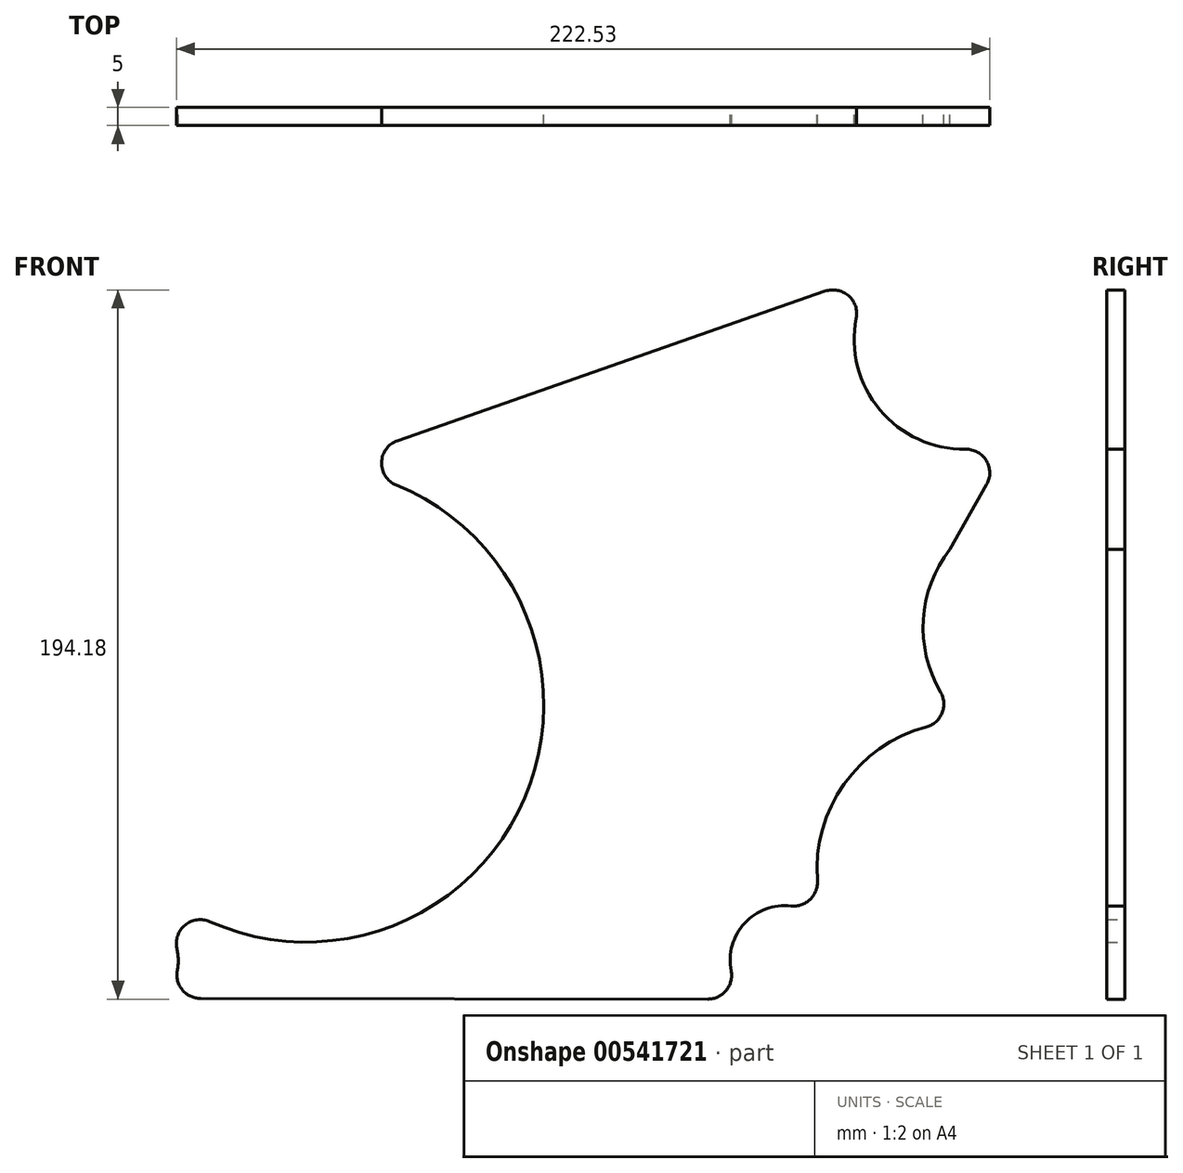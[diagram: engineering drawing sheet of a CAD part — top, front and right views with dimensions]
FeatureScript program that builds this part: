
annotation { "Feature Type Name" : "Feature", "Feature Type Description" : "" }
export const myFeature = defineFeature(function(context is Context, id is Id, definition is map)
    precondition{}
    {
        {
            var Q0;
            Q0=qCreatedBy(makeId("Front.planeOp"),FACE);
            var sketch = newSketch(context, id + "F0", { "sketchPlane" : qUnion([Q0])});
            skCircle(sketch, "E0", {"center": v(0, 0) * mm, "radius": 60 * mm});
            skCircle(sketch, "E1", {"center": v(-24.58, 0) * mm, "radius": 5 * mm});
            skCircle(sketch, "E2.1.0", {"center": v(-12.3, -21.3) * mm, "radius": 5 * mm});
            skCircle(sketch, "E2.2.0", {"center": v(12.3, -21.3) * mm, "radius": 5 * mm});
            skCircle(sketch, "E2.3.0", {"center": v(24.58, 0) * mm, "radius": 5 * mm});
            skCircle(sketch, "E2.4.0", {"center": v(12.3, 21.3) * mm, "radius": 5 * mm});
            skCircle(sketch, "E2.5.0", {"center": v(-12.3, 21.3) * mm, "radius": 5 * mm});
            skLineSegment(sketch, "E3", {"start": v(0, 0) * mm, "end": v(78.97, 13.92) * mm, "construction": true});
            skArc(sketch, "E4", {"start": v(44.32, 7.81) * mm, "mid": v(50.1, 3.76) * mm, "end": v(54.16, 9.55) * mm});
            skLineSegment(sketch, "E5", {"start": v(0, 0) * mm, "end": v(13.1, 74.28) * mm, "construction": true});
            skArc(sketch, "E6", {"start": v(9.55, 54.16) * mm, "mid": v(3.76, 50.1) * mm, "end": v(7.81, 44.32) * mm});
            skArc(sketch, "E7", {"start": v(9.55, 54.16) * mm, "mid": v(38.9, 38.9) * mm, "end": v(54.16, 9.55) * mm});
            skArc(sketch, "E8", {"start": v(7.81, 44.32) * mm, "mid": v(31.82, 31.82) * mm, "end": v(44.32, 7.81) * mm});
            skArc(sketch, "E9.MirrorCS", {"start": v(-9.55, 54.16) * mm, "mid": v(-38.9, 38.9) * mm, "end": v(-54.16, 9.55) * mm});
            skArc(sketch, "E10.MirrorCS", {"start": v(-7.81, 44.32) * mm, "mid": v(-31.82, 31.82) * mm, "end": v(-44.32, 7.81) * mm});
            skArc(sketch, "E11.MirrorCS", {"start": v(-44.32, 7.81) * mm, "mid": v(-50.1, 3.76) * mm, "end": v(-54.16, 9.55) * mm});
            skArc(sketch, "E12.MirrorCS", {"start": v(-9.55, 54.16) * mm, "mid": v(-3.76, 50.1) * mm, "end": v(-7.81, 44.32) * mm});
            skArc(sketch, "E13.MirrorCS", {"start": v(-7.81, -44.32) * mm, "mid": v(-31.82, -31.82) * mm, "end": v(-44.32, -7.81) * mm});
            skArc(sketch, "E14.MirrorCS", {"start": v(-9.55, -54.16) * mm, "mid": v(-38.9, -38.9) * mm, "end": v(-54.16, -9.55) * mm});
            skArc(sketch, "E15.MirrorCS", {"start": v(-44.32, -7.81) * mm, "mid": v(-50.1, -3.76) * mm, "end": v(-54.16, -9.55) * mm});
            skArc(sketch, "E16.MirrorCS", {"start": v(-9.55, -54.16) * mm, "mid": v(-3.76, -50.1) * mm, "end": v(-7.81, -44.32) * mm});
            skArc(sketch, "E17.MirrorCS", {"start": v(9.55, -54.16) * mm, "mid": v(3.76, -50.1) * mm, "end": v(7.81, -44.32) * mm});
            skArc(sketch, "E18.MirrorCS", {"start": v(7.81, -44.32) * mm, "mid": v(31.82, -31.82) * mm, "end": v(44.32, -7.81) * mm});
            skArc(sketch, "E19.MirrorCS", {"start": v(9.55, -54.16) * mm, "mid": v(38.9, -38.9) * mm, "end": v(54.16, -9.55) * mm});
            skArc(sketch, "E20.MirrorCS", {"start": v(44.32, -7.81) * mm, "mid": v(50.1, -3.76) * mm, "end": v(54.16, -9.55) * mm});
            skLineSegment(sketch, "E21", {"start": v(180, 112.63) * mm, "end": v(180, -76.66) * mm, "construction": true});
            skLineSegment(sketch, "E22", {"start": v(-74.83, 0) * mm, "end": v(210.53, 0) * mm, "construction": true});
            skCircle(sketch, "E23", {"center": v(180, 100) * mm, "radius": 25 * mm});
            skCircle(sketch, "E24", {"center": v(180, -45) * mm, "radius": 35 * mm});
            skArc(sketch, "E25", {"start": v(-21.46, 61.35) * mm, "mid": v(-53.01, 37.62) * mm, "end": v(-65, 0) * mm});
            skArc(sketch, "E26", {"start": v(150.52, 105.8) * mm, "mid": v(156.92, 80.75) * mm, "end": v(180.43, 69.95) * mm});
            skArc(sketch, "E27", {"start": v(169.62, -6.12) * mm, "mid": v(147.16, -21.75) * mm, "end": v(139.88, -48.13) * mm});
            skLineSegment(sketch, "E28", {"start": v(-21.46, 61.35) * mm, "end": v(170.08, 128.36) * mm});
            skLineSegment(sketch, "E29", {"start": v(24.98, 72.3) * mm, "end": v(142, 113.2) * mm});
            skPoint(sketch, "E30.visualSharp", {"position": v(3.8, 64.89) * mm});
            skArc(sketch, "E30.filletArc", {"start": v(24.98, 72.3) * mm, "mid": v(20.62, 66.33) * mm, "end": v(24.66, 60.14) * mm});
            skPoint(sketch, "E31.visualSharp", {"position": v(156, 118.1) * mm});
            skArc(sketch, "E31.filletArc", {"start": v(150.52, 105.8) * mm, "mid": v(148.4, 111.97) * mm, "end": v(142, 113.2) * mm});
            skArc(sketch, "E32", {"start": v(180, 39.38) * mm, "mid": v(175, 12.66) * mm, "end": v(193.63, -7.13) * mm});
            skLineSegment(sketch, "E33.trimOffspring", {"start": v(177.8, 36.1) * mm, "end": v(206.02, 84.97) * mm});
            skArc(sketch, "E34", {"start": v(176.1, 42.5) * mm, "mid": v(168.86, 23.36) * mm, "end": v(173.56, 3.44) * mm});
            skLineSegment(sketch, "E35", {"start": v(201.88, 87.91) * mm, "end": v(201.6, 87.4) * mm});
            skLineSegment(sketch, "E36.trimOffspring", {"start": v(186.17, 60.24) * mm, "end": v(176.1, 42.5) * mm});
            skArc(sketch, "E37.trimOffspring", {"start": v(206.02, 84.97) * mm, "mid": v(203.14, 119.17) * mm, "end": v(170.08, 128.36) * mm});
            skPoint(sketch, "E38.visualSharp", {"position": v(193.5, 73.15) * mm});
            skArc(sketch, "E38.filletArc", {"start": v(186.17, 60.24) * mm, "mid": v(186.11, 66.76) * mm, "end": v(180.43, 69.95) * mm});
            skPoint(sketch, "E39.visualSharp", {"position": v(180.19, -4.76) * mm});
            skArc(sketch, "E39.filletArc", {"start": v(169.62, -6.12) * mm, "mid": v(173.96, -2.31) * mm, "end": v(173.56, 3.44) * mm});
            skArc(sketch, "E40", {"start": v(-35.25, -72.75) * mm, "mid": v(-35, -69.75) * mm, "end": v(-35.35, -66.76) * mm});
            skArc(sketch, "E41", {"start": v(132.67, -55.1) * mm, "mid": v(119.97, -59.83) * mm, "end": v(116.28, -72.87) * mm});
            skCircle(sketch, "E42", {"center": v(131, -70) * mm, "radius": 4.25 * mm});
            skCircle(sketch, "E43", {"center": v(-50, -70) * mm, "radius": 4.25 * mm});
            skLineSegment(sketch, "E44", {"start": v(-51.13, -84.96) * mm, "end": v(179.95, -85.24) * mm});
            skLineSegment(sketch, "E45", {"start": v(-28.87, -80.44) * mm, "end": v(109.89, -80.62) * mm});
            skArc(sketch, "E46.trimOffspring", {"start": v(179.95, -85.24) * mm, "mid": v(219.64, -51.94) * mm, "end": v(193.63, -7.13) * mm});
            skPoint(sketch, "E47.visualSharp", {"position": v(145.23, -65.27) * mm});
            skArc(sketch, "E47.filletArc", {"start": v(132.67, -55.1) * mm, "mid": v(137.92, -53.3) * mm, "end": v(139.88, -48.13) * mm});
            skPoint(sketch, "E48.visualSharp", {"position": v(120.42, -80.63) * mm});
            skArc(sketch, "E48.filletArc", {"start": v(109.89, -80.62) * mm, "mid": v(114.91, -78.25) * mm, "end": v(116.28, -72.87) * mm});
            skLineSegment(sketch, "E49", {"start": v(-65, 0) * mm, "end": v(-65, -70) * mm});
            skArc(sketch, "E50", {"start": v(-26.37, -59.4) * mm, "mid": v(-33.12, -60.32) * mm, "end": v(-35.35, -66.76) * mm});
            skArc(sketch, "E51.trimOffspring", {"start": v(-65, -70) * mm, "mid": v(-60.21, -80.99) * mm, "end": v(-48.9, -84.96) * mm});
            skArc(sketch, "E52.trimOffspring", {"start": v(-26.37, -59.4) * mm, "mid": v(59.78, -25.52) * mm, "end": v(24.66, 60.14) * mm});
            skPoint(sketch, "E53.visualSharp", {"position": v(-39.22, -80.43) * mm});
            skArc(sketch, "E53.filletArc", {"start": v(-35.25, -72.75) * mm, "mid": v(-33.87, -78.1) * mm, "end": v(-28.87, -80.44) * mm});
            skSolve(sketch);
        }
        {
            var Q0;
            Q0=makeQuery(id+"F0.imprint","IMPRINT",FACE,{"disambiguationData":[TD([[makeQuery(id+"F0.imprint","IMPRINT",EDGE,{"derivedFrom":sQuery(id+"F0.wireOp",EDGE,"E26")}),-1.0]])]});
            extrude(context, id + "F1", {"entities" : qUnion([Q0]), "depth" : 5 * mm, "offsetDistance" : 25 * mm});
        }
    });
